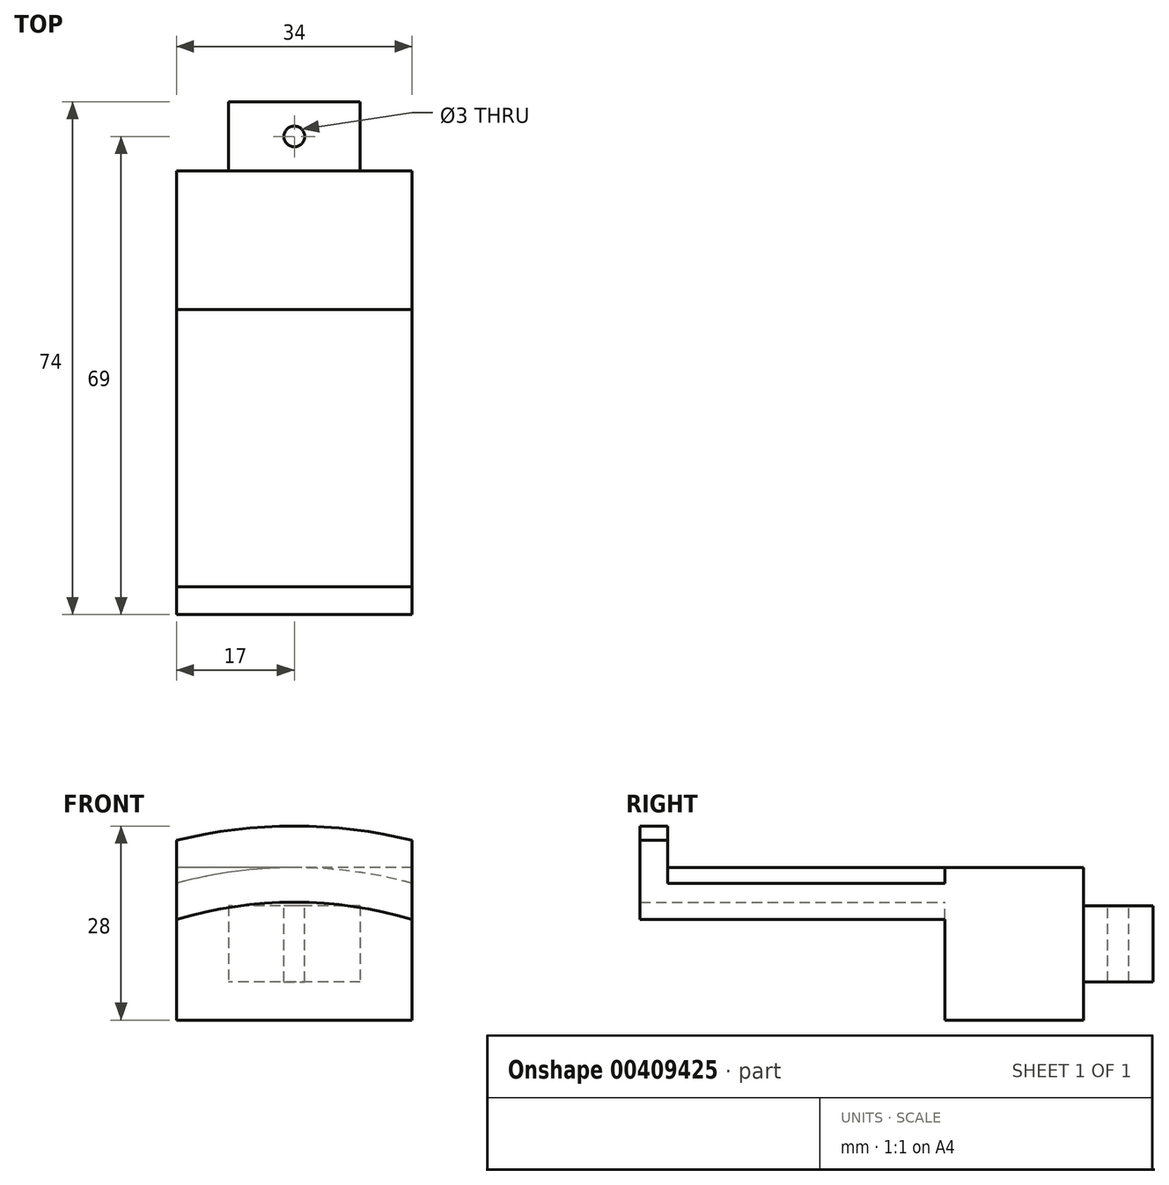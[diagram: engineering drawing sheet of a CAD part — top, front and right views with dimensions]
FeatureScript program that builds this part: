
annotation { "Feature Type Name" : "Feature", "Feature Type Description" : "" }
export const myFeature = defineFeature(function(context is Context, id is Id, definition is map)
    precondition{}
    {
        {
            var Q0;
            Q0=qCreatedBy(makeId("Front.planeOp"),FACE);
            var sketch = newSketch(context, id + "F0", { "sketchPlane" : qUnion([Q0])});
            skLineSegment(sketch, "E0.bottom", {"start": v(9.5, 5.5) * mm, "end": v(-9.5, 5.5) * mm});
            skLineSegment(sketch, "E0.top", {"start": v(9.5, -5.5) * mm, "end": v(-9.5, -5.5) * mm});
            skLineSegment(sketch, "E0.left", {"start": v(9.5, 5.5) * mm, "end": v(9.5, -5.5) * mm});
            skLineSegment(sketch, "E0.right", {"start": v(-9.5, 5.5) * mm, "end": v(-9.5, -5.5) * mm});
            skPoint(sketch, "E0.middle", {"position": v(0, 0) * mm});
            skSolve(sketch);
        }
        {
            var Q0;
            Q0 = qSketchRegion(id + "F0", true);
            extrude(context, id + "F1", {"entities" : qUnion([Q0]), "depth" : 10 * mm, "offsetDistance" : 25 * mm});
        }
        {
            var Q0;
            Q0=makeQuery(id+"F1.opExtrude","CAP_FACE",FACE,{"disambiguationData":[OSD([sQuery(id+"F0.wireOp",EDGE,"E0.bottom"),sQuery(id+"F0.wireOp",EDGE,"E0.top"),sQuery(id+"F0.wireOp",EDGE,"E0.left"),sQuery(id+"F0.wireOp",EDGE,"E0.right")])],"isStart":false});
            var sketch = newSketch(context, id + "F2", { "sketchPlane" : qUnion([Q0])});
            skLineSegment(sketch, "E1.bottom", {"start": v(17, 11) * mm, "end": v(-17, 11) * mm});
            skLineSegment(sketch, "E1.top", {"start": v(17, -11) * mm, "end": v(-17, -11) * mm});
            skLineSegment(sketch, "E1.left", {"start": v(17, 11) * mm, "end": v(17, -11) * mm});
            skLineSegment(sketch, "E1.right", {"start": v(-17, 11) * mm, "end": v(-17, -11) * mm});
            skPoint(sketch, "E1.middle", {"position": v(0, 0) * mm});
            skSolve(sketch);
        }
        {
            var Q0;
            Q0 = qSketchRegion(id + "F2", true);
            extrude(context, id + "F3", {"entities" : qUnion([Q0]), "operationType" : NewBodyOperationType.ADD, "depth" : 20 * mm, "offsetDistance" : 25 * mm});
        }
        {
            var Q0;
            Q0=makeQuery(id+"F3.opExtrude","CAP_FACE",FACE,{"disambiguationData":[OSD([sQuery(id+"F2.wireOp",EDGE,"E1.bottom"),sQuery(id+"F2.wireOp",EDGE,"E1.top"),sQuery(id+"F2.wireOp",EDGE,"E1.left"),sQuery(id+"F2.wireOp",EDGE,"E1.right")])],"isStart":false});
            var sketch = newSketch(context, id + "F4", { "sketchPlane" : qUnion([Q0])});
            skLineSegment(sketch, "E2", {"start": v(-24.42, -54) * mm, "end": v(26.64, -54) * mm, "construction": true});
            skArc(sketch, "E3", {"start": v(17, 8.74) * mm, "mid": v(0, 11) * mm, "end": v(-17, 8.74) * mm});
            skArc(sketch, "E4", {"start": v(17, 3.54) * mm, "mid": v(0, 6) * mm, "end": v(-17, 3.54) * mm});
            skLineSegment(sketch, "E5", {"start": v(17, 3.54) * mm, "end": v(17, 8.74) * mm});
            skLineSegment(sketch, "E6", {"start": v(-17, 0) * mm, "end": v(-17, 8.74) * mm});
            skSolve(sketch);
        }
        {
            var Q0;
            Q0 = qSketchRegion(id + "F4", true);
            extrude(context, id + "F5", {"entities" : qUnion([Q0]), "operationType" : NewBodyOperationType.ADD, "depth" : 40 * mm, "offsetDistance" : 25 * mm});
        }
        {
            var Q0;
            Q0=makeQuery(id+"F5.opExtrude","CAP_FACE",FACE,{"disambiguationData":[OSD([sQuery(id+"F4.wireOp",EDGE,"E3"),sQuery(id+"F4.wireOp",EDGE,"E4"),sQuery(id+"F4.wireOp",EDGE,"E5"),sQuery(id+"F4.wireOp",EDGE,"E6")])],"isStart":false});
            var sketch = newSketch(context, id + "F6", { "sketchPlane" : qUnion([Q0])});
            skArc(sketch, "E7.0.0", {"start": v(-17, 3.54) * mm, "mid": v(0, 6) * mm, "end": v(17, 3.54) * mm});
            skLineSegment(sketch, "E7.0.1", {"start": v(17, 3.54) * mm, "end": v(17, 8.74) * mm});
            skLineSegment(sketch, "E7.0.3", {"start": v(-17, 8.74) * mm, "end": v(-17, 3.54) * mm});
            skLineSegment(sketch, "E8", {"start": v(-17, 8.74) * mm, "end": v(-17, 14.93) * mm});
            skLineSegment(sketch, "E9", {"start": v(17, 8.74) * mm, "end": v(17, 14.93) * mm});
            skArc(sketch, "E10.0", {"start": v(17, 14.93) * mm, "mid": v(0, 17) * mm, "end": v(-17, 14.93) * mm});
            skSolve(sketch);
        }
        {
            var Q0;
            Q0 = qSketchRegion(id + "F6", true);
            extrude(context, id + "F7", {"entities" : qUnion([Q0]), "operationType" : NewBodyOperationType.ADD, "depth" : 4 * mm, "offsetDistance" : 25 * mm});
        }
        {
            var Q0;
            Q0=makeQuery(id+"F1.opExtrude","SWEPT_FACE",FACE,{"disambiguationData":[OSD([sQuery(id+"F0.wireOp",EDGE,"E0.bottom")])]});
            var sketch = newSketch(context, id + "F8", { "sketchPlane" : qUnion([Q0])});
            skCircle(sketch, "E11", {"center": v(0, -5) * mm, "radius": 1.5 * mm});
            skSolve(sketch);
        }
        {
            var Q0;
            Q0 = qSketchRegion(id + "F8", true);
            extrude(context, id + "F9", {"entities" : qUnion([Q0]), "operationType" : NewBodyOperationType.REMOVE, "endBound" : BoundingType.THROUGH_ALL, "oppositeDirection" : true, "depth" : 25 * mm, "offsetDistance" : 25 * mm});
        }
    });
